# Revit family: Camera-Security-Panasonic-Super_Dynamic_FullHD-PTZ-Dome-Network-S6131Series(VV)X
name_source: partatom
category: Security Devices
revit_build: Autodesk Revit 2016 (Build: 20150714_1515(x64)
units: mm (PartAtom-declared; Revit-internal decimal feet)

## family parameters
Cut with Voids When Loaded = No
Host = Face
Maintain Annotation Orientation = No
OmniClass Number = 23.85.10.14.11
OmniClass Title = Cameras
Part Type = Normal
Room Calculation Point = No
Round Connector Dimension = Use Diameter
Shared = No

## types (2) — shared parameters
Alarm Input Or Output Specification = ALARM IN 1 (Black & white input, Auto time adjustment input) (x1), ALARM IN 2 (ALARM OUT) (x1), ALARM IN 3 (AUX OUT) (x1)
Angle Of View = 66.0
Audio In = Yes
Audio Out = Yes
Communication Ports = 10Base-T / 100Base-TX, RJ-45
Date Last Modified = August 1, 2017
Day Or Night = Yes
Default Elevation = 48 "
Diameter = 7.283 "
Equipment Abbreviation = SC
Family Version = 1.0.0
HFOV Max 169 = 66.00°
HFOV Max 43 = 51.00°
HFOV Min 169 = 1.90°
HFOV Min 43 = 1.40°
Has POE = Yes
Height = 8.425 "
IP Or Analog = IP
Indoor Or Outdoor = Indoor
Manufacturer = Panasonic
Model Disclaimer = Contact Panasonic for more information
Mounting Positions = Mount Dependent
Operational Humidity = 10 to 90 % (no condensation)
Operational Temperature = 14°F - 122°F
Pan Max = 360.00°
Pan Min = 0.00°
Panning Range = 360
Power Active = 12.0 W
Product Documentation Link = http://ssbu-t.psn-web.net
Product Material = Paint - Panasonic - Sail White
Product Page URL = http://security.panasonic.com
Provide Feedback = https://www.surveymonkey.com
Regulatory Compliance = UL60950-1, C-UL CAN/CSA C22.2 No.60950-1, CE, IEC60950-1, FCC Part15 Class A, ICES-003 Class A, EN55022 Class B, EN55024
Storage Temperature = 14°F - 122°F
Tilt Max = 205.00°
Tilt Min = -25.00°
Tilting Range = -25 to +205
URL = http://security.panasonic.com
VFOV Max 169 = 39.00°
VFOV Max 43 = 39.00°
VFOV Min 169 = 1.10°
VFOV Min 43 = 1.10°
Vandal Resistant = No
Voltage DC = 12 V
Weight = 3.84 lb
Wide Dynamic Range = Yes
z Const Pan Handle Length = 27.559 "
z Const Tilt Base Length = 9.843 "
z Const Tilt Base2 Length = 19.685 "
z Const Tilt Handle Length = 14.173 "
z Const Yaw Base Length = 10.236 "
z Const Yaw Base2 Length = 17.323 "
z Const Yaw Handle Length = 9.252 "
z VV Viewpoint Depth Max = 2.106 "
z VV Viewpoint Depth Min = 2.106 "
zero-valued in all types: PPM Target Height

## per-type parameters (varying)
| type | Description | Minimum Illumination | Model | Part Description | Part Number | z Camera Type |
| Standard, WV-S6131 | Security Camera, H.264/H.265, Super Dynamic ,Full HD, 21x Optical Zoom, Indoor, PTZ, Network, WV-S6131 | 0.015 lx | WV-S6131 | Security Camera, H.264/H.265, Super Dynamic ,Full HD, 21x Optical Zoom, Indoor, PTZ, Network, WV-S6131 | WV-S6131 | 1 |
| Standard, WV-S6111 | Security Camera, H.264/H.265, Super Dynamic ,HD, 21x Optical Zoom, Indoor, PTZ, Network, WV-S6111 | 0.011 lx | WV-S6111 | Security Camera, H.264/H.265, Super Dynamic ,HD, 21x Optical Zoom, Indoor, PTZ, Network, WV-S6111 | WV-S6111 | 2 |

## geometry (parser evidence)
native form markers: Blend x4, Sweep x7
no freeform markers — native parametric forms only
